# Revit family: P200548KD-030c_KDTE304LPA
name_source: partatom
category: Specialty Equipment
units: mm (PartAtom-declared; Revit-internal decimal feet)

## family parameters
Always vertical = Yes
Cut with Voids When Loaded = No
Enable Cutting in Views = No
Maintain Annotation Orientation = No
Part Type = Normal
Room Calculation Point = No
Round Connector Dimension = Use Diameter
Shared = No
Work Plane-Based = No

## types (1)
- KDTE304LPA
    Accent Material = ARCAT - Metal - Steel - Black
    Amps = 0 A
    Base Fitting Material = ARCAT - Metal - Plastic - Cream
    Blanket Material = ARCAT - Fabric - Grey
    Body Material = ARCAT - Metal - Plastic - Grey
    Bottom Panel Material = ARCAT - Metal - Steel - Black
    Clearance Material = ARCAT - Clearance
    Default Elevation = 0"
    Depth = 28 1/2"
    Display Panel Material = ARCAT - Glass - Black
    Door Material = ARCAT - Metal - Steel - Grey
    Family Name = Dishwasher
    Handle Material = ARCAT - Metal - Steel - Stainless
    Height = 34"
    Manufacturer = KitchenAid
    Model = KDTE304LPA
    Voltage = 0 V
    Width = 24 1/2"

## geometry (parser evidence)
native form markers: Sweep x3
no freeform markers — native parametric forms only
